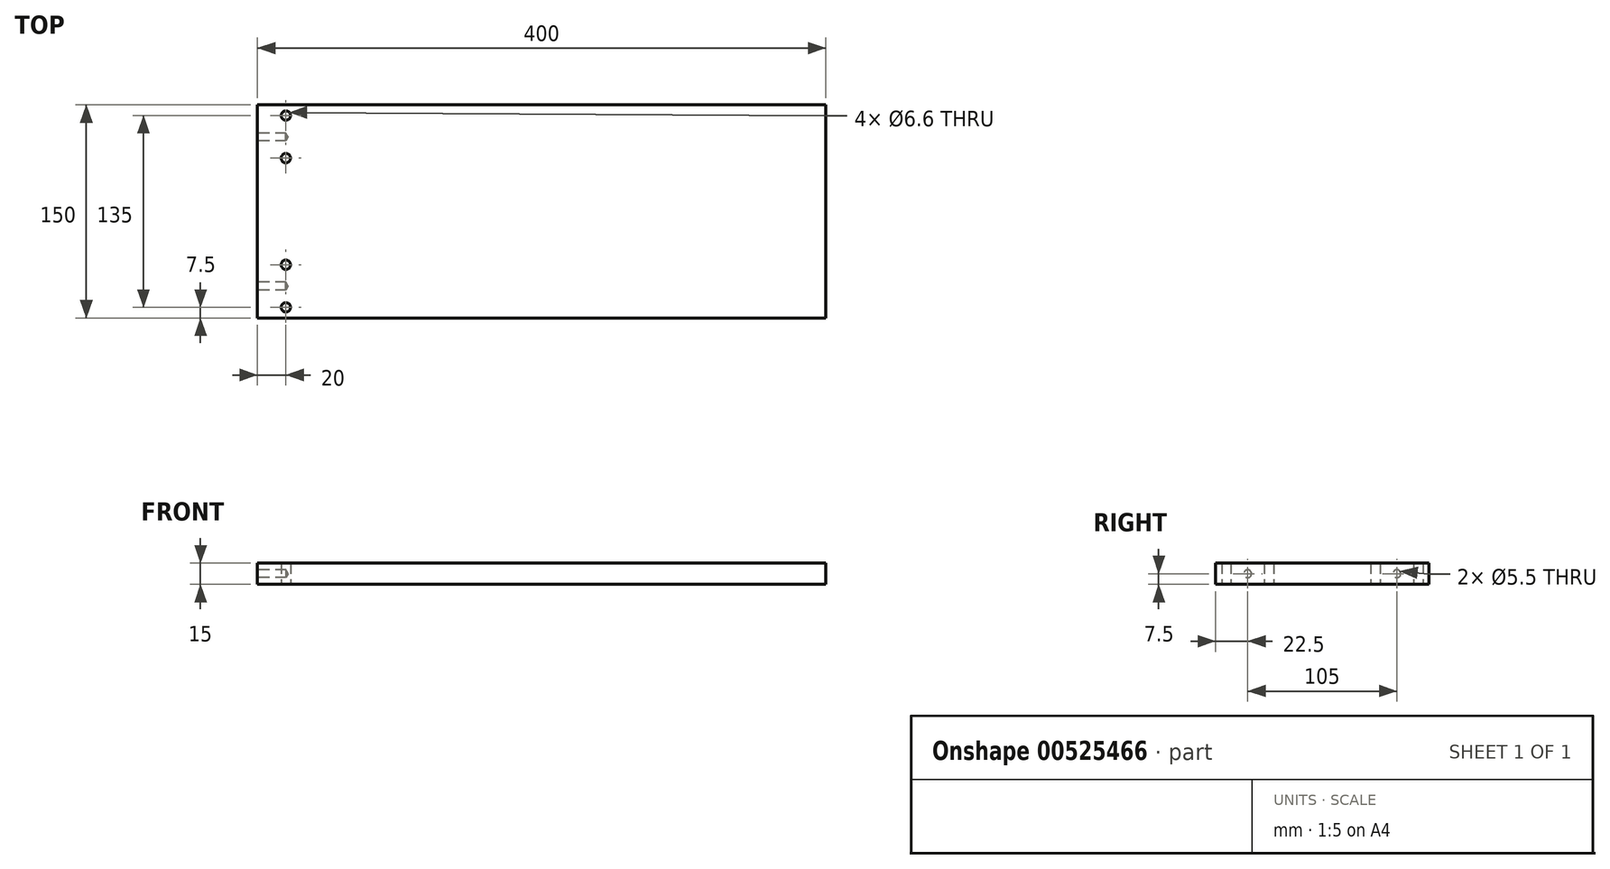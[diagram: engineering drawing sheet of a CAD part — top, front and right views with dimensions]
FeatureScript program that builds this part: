
annotation { "Feature Type Name" : "Feature", "Feature Type Description" : "" }
export const myFeature = defineFeature(function(context is Context, id is Id, definition is map)
    precondition{}
    {
        {
            var Q0;
            Q0=qCreatedBy(makeId("Top.planeOp"),FACE);
            var sketch = newSketch(context, id + "F0", { "sketchPlane" : qUnion([Q0])});
            skLineSegment(sketch, "E0.bottom", {"start": v(200, 75) * mm, "end": v(-200, 75) * mm});
            skLineSegment(sketch, "E0.top", {"start": v(200, -75) * mm, "end": v(-200, -75) * mm});
            skLineSegment(sketch, "E0.left", {"start": v(200, 75) * mm, "end": v(200, -75) * mm});
            skLineSegment(sketch, "E0.right", {"start": v(-200, 75) * mm, "end": v(-200, -75) * mm});
            skPoint(sketch, "E0.middle", {"position": v(0, 0) * mm});
            skPoint(sketch, "E1", {"position": v(-180, 67.5) * mm});
            skPoint(sketch, "E2", {"position": v(-180, 37.5) * mm});
            skPoint(sketch, "E3", {"position": v(-180, -37.5) * mm});
            skPoint(sketch, "E4", {"position": v(-180, -67.5) * mm});
            skSolve(sketch);
        }
        {
            var Q0;
            Q0=makeQuery(id+"F0.imprint","IMPRINT",FACE,{"disambiguationData":[TD([[makeQuery(id+"F0.imprint","IMPRINT",EDGE,{"derivedFrom":sQuery(id+"F0.wireOp",EDGE,"E0.bottom")}),1.0]])]});
            extrude(context, id + "F1", {"entities" : qUnion([Q0]), "depth" : 15 * mm, "offsetDistance" : 25 * mm});
        }
        {
            var Q0;
            Q0=sQuery(id+"F0.wireOp",VERTEX,"E2");
            var Q1;
            Q1=sQuery(id+"F0.wireOp",VERTEX,"E1");
            var Q2;
            Q2=sQuery(id+"F0.wireOp",VERTEX,"E3");
            var Q3;
            Q3=sQuery(id+"F0.wireOp",VERTEX,"E4");
            var Q4;
            Q4=makeQuery(id+"F1.opExtrude","SWEPT_BODY",BODY,{"disambiguationData":[OSD([sQuery(id+"F0.wireOp",EDGE,"E0.bottom"),sQuery(id+"F0.wireOp",EDGE,"E0.top"),sQuery(id+"F0.wireOp",EDGE,"E0.left"),sQuery(id+"F0.wireOp",EDGE,"E0.right")])]});
            hole(context, id + "F2", {"style" : HoleStyle.SIMPLE, "endStyle" : HoleEndStyle.THROUGH, "oppositeDirection" : true, "standardTappedOrClearance" : lookupTablePath({ "standard" : "ISO", "fit" : "Normal", "size" : "M6", "type" : "Clearance" }), "standardBlindInLast" : lookupTablePath({ "fit" : "Standard", "standard" : "ISO", "size" : "M6", "type" : "Clearance" }), "holeDiameter" : 6.6 * mm, "isTappedThrough" : true, "tappedDepth" : 12 * mm, "tapClearance" : 3, "locations" : qUnion([Q0, Q1, Q2, Q3]), "scope" : qUnion([Q4])});
        }
        {
            var Q0;
            Q0=makeQuery(id+"F1.opExtrude","SWEPT_FACE",FACE,{"disambiguationData":[OSD([sQuery(id+"F0.wireOp",EDGE,"E0.right")])]});
            var sketch = newSketch(context, id + "F3", { "sketchPlane" : qUnion([Q0])});
            skPoint(sketch, "E5", {"position": v(-52.5, 7.5) * mm});
            skPoint(sketch, "E6", {"position": v(52.5, 7.5) * mm});
            skSolve(sketch);
        }
        {
            var Q0;
            Q0=sQuery(id+"F3.wireOp",VERTEX,"E5");
            var Q1;
            Q1=sQuery(id+"F3.wireOp",VERTEX,"E6");
            var Q2;
            Q2=makeQuery(id+"F1.opExtrude","SWEPT_BODY",BODY,{"disambiguationData":[OSD([sQuery(id+"F0.wireOp",EDGE,"E0.bottom"),sQuery(id+"F0.wireOp",EDGE,"E0.top"),sQuery(id+"F0.wireOp",EDGE,"E0.left"),sQuery(id+"F0.wireOp",EDGE,"E0.right")])]});
            hole(context, id + "F4", {"style" : HoleStyle.SIMPLE, "endStyle" : HoleEndStyle.BLIND, "standardTappedOrClearance" : lookupTablePath({ "standard" : "ISO", "fit" : "Normal", "size" : "M5", "type" : "Clearance" }), "standardBlindInLast" : lookupTablePath({ "fit" : "Standard", "standard" : "ISO", "size" : "M5", "type" : "Clearance" }), "holeDiameter" : 5.5 * mm, "holeDepth" : 20 * mm, "isTappedThrough" : true, "tappedDepth" : 12 * mm, "tapClearance" : 3, "locations" : qUnion([Q0, Q1]), "scope" : qUnion([Q2])});
        }
    });
